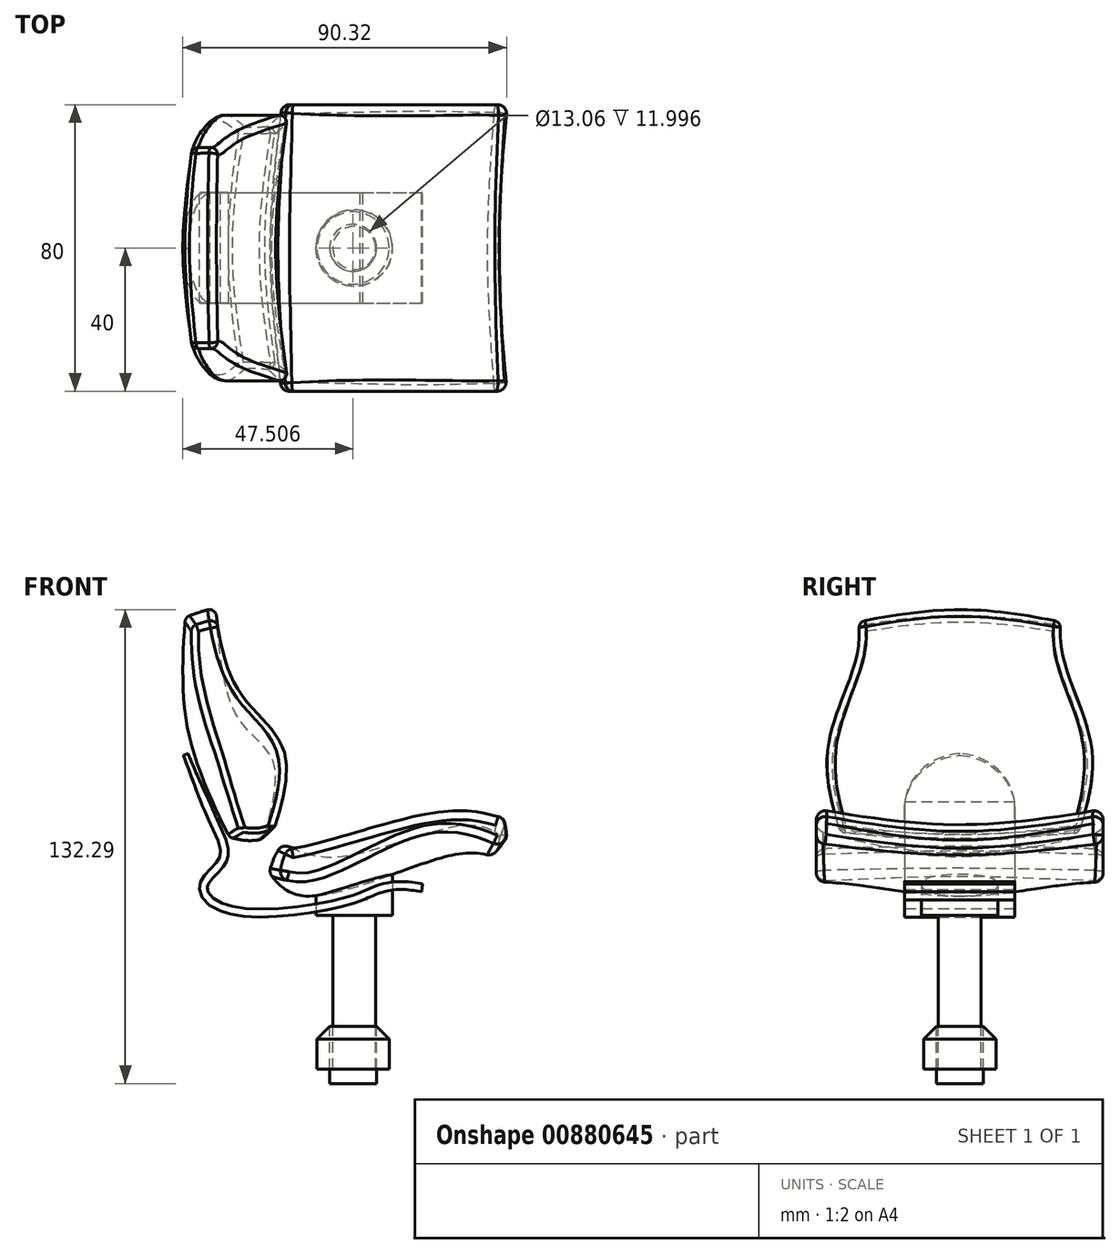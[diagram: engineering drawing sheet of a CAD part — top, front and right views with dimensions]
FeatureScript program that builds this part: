
annotation { "Feature Type Name" : "Feature", "Feature Type Description" : "" }
export const myFeature = defineFeature(function(context is Context, id is Id, definition is map)
    precondition{}
    {
        {
            var Q0;
            Q0=qCreatedBy(makeId("Front.planeOp"),FACE);
            var sketch = newSketch(context, id + "F0", { "sketchPlane" : qUnion([Q0])});
            skFitSpline(sketch, "E0", {"points": [v(-29.7, 59.89) * mm, v(-23.34, 27.8) * mm, v(-13.8, 16.24) * mm, v(-16.4, -6.3) * mm], "startDerivative": vector(6.88, -94.05) * mm, "endDerivative": vector(-21.45, -77.38) * mm});
            skFitSpline(sketch, "E1", {"points": [v(-37.8, 60.76) * mm, v(-37.5, 25.2) * mm, v(-25.36, -6.3) * mm], "startDerivative": vector(-5.51, -71.82) * mm, "endDerivative": vector(30.53, -62.27) * mm});
            skFitSpline(sketch, "E2", {"points": [v(-21.32, 59.89) * mm, v(-33.75, 57.58) * mm, v(-49.07, 50.93) * mm], "startDerivative": vector(-26.27, -3.23) * mm, "endDerivative": vector(-29.17, -14.43) * mm});
            skFitSpline(sketch, "E3", {"points": [v(-37.8, 0) * mm, v(-19.58, -6.3) * mm, v(-4.55, 0) * mm], "startDerivative": vector(35.9, -18.7) * mm, "endDerivative": vector(30.52, 19.22) * mm});
            skSolve(sketch);
        }
        {
            var Q0;
            Q0=qCreatedBy(makeId("Front.planeOp"),FACE);
            cPlane(context, id + "F1", {"entities" : qUnion([Q0]), "cplaneType" : CPlaneType.OFFSET, "offset" : 40 * mm, "width" : 150 * mm, "height" : 150 * mm});
        }
        {
            var Q0;
            Q0=qCreatedBy(id+"F1.planeOp",FACE);
            var sketch = newSketch(context, id + "F2", { "sketchPlane" : qUnion([Q0])});
            skFitSpline(sketch, "E4", {"points": [v(-32.08, 63.62) * mm, v(-23.6, 39.46) * mm, v(-9.8, 19.21) * mm, v(-15.3, -10.6) * mm], "startDerivative": vector(17.6, -78.26) * mm, "endDerivative": vector(-33.1, -90.51) * mm});
            skFitSpline(sketch, "E5", {"points": [v(-35.53, 62.05) * mm, v(-32.08, 31.45) * mm, v(-19.06, -10.92) * mm], "startDerivative": vector(3.9, -64.95) * mm, "endDerivative": vector(28.32, -80.51) * mm});
            skFitSpline(sketch, "E6", {"points": [v(-45.73, 44.8) * mm, v(-31.61, 52) * mm, v(-18.74, 51.23) * mm], "startDerivative": vector(26.78, 17.77) * mm, "endDerivative": vector(27.2, -5.3) * mm});
            skFitSpline(sketch, "E7", {"points": [v(-31.77, 0) * mm, v(-17.24, -3.37) * mm, v(-7.03, 1.29) * mm], "startDerivative": vector(28.52, -10.67) * mm, "endDerivative": vector(20.78, 13.83) * mm});
            skSolve(sketch);
        }
        {
            var Q0;
            Q0=qCreatedBy(makeId("Front.planeOp"),FACE);
            cPlane(context, id + "F3", {"entities" : qUnion([Q0]), "cplaneType" : CPlaneType.OFFSET, "offset" : 40 * mm, "oppositeDirection" : true, "width" : 150 * mm, "height" : 150 * mm});
        }
        {
            var Q0;
            Q0=qCreatedBy(id+"F3.planeOp",FACE);
            var sketch = newSketch(context, id + "F4", { "sketchPlane" : qUnion([Q0])});
            skFitSpline(sketch, "E8", {"points": [v(-32.11, 63.62) * mm, v(-23.64, 39.46) * mm, v(-9.83, 19.21) * mm, v(-15.32, -10.6) * mm], "startDerivative": vector(17.6, -78.26) * mm, "endDerivative": vector(-33.1, -90.51) * mm});
            skFitSpline(sketch, "E9", {"points": [v(-35.56, 62.05) * mm, v(-32.11, 31.45) * mm, v(-19.09, -10.92) * mm], "startDerivative": vector(3.9, -64.95) * mm, "endDerivative": vector(28.32, -80.51) * mm});
            skFitSpline(sketch, "E10", {"points": [v(-45.76, 44.8) * mm, v(-31.64, 52) * mm, v(-18.77, 51.23) * mm], "startDerivative": vector(26.78, 17.77) * mm, "endDerivative": vector(27.2, -5.3) * mm});
            skFitSpline(sketch, "E11", {"points": [v(-31.8, 0) * mm, v(-17.27, -3.37) * mm, v(-7.06, 1.29) * mm], "startDerivative": vector(28.52, -10.67) * mm, "endDerivative": vector(20.78, 13.83) * mm});
            skSolve(sketch);
        }
        {
            var Q0;
            {var subQ0=sQuery(id+"F2.wireOp",EDGE,"E6");var subQ1=sQuery(id+"F2.wireOp",EDGE,"E4");var subQ2=makeQuery(id+"F2.imprint","INTERSECT",VERTEX,{"derivedFrom":[subQ1,subQ0]});Q0=makeQuery(id+"F2.imprint","IMPRINT",FACE,{"disambiguationData":[TD([[makeQuery(id+"F2.imprint","IMPRINT",EDGE,{"disambiguationData":[TD([[subQ2,-1.0]])],"derivedFrom":subQ1}),-1.0]])]});}
            var Q1;
            {var subQ0=sQuery(id+"F0.wireOp",EDGE,"E2");var subQ1=sQuery(id+"F0.wireOp",EDGE,"E0");var subQ2=makeQuery(id+"F0.imprint","INTERSECT",VERTEX,{"derivedFrom":[subQ1,subQ0]});Q1=makeQuery(id+"F0.imprint","IMPRINT",FACE,{"disambiguationData":[TD([[makeQuery(id+"F0.imprint","IMPRINT",EDGE,{"disambiguationData":[TD([[subQ2,-1.0]])],"derivedFrom":subQ1}),-1.0]])]});}
            var Q2;
            {var subQ0=sQuery(id+"F4.wireOp",EDGE,"E10");var subQ1=sQuery(id+"F4.wireOp",EDGE,"E8");var subQ2=makeQuery(id+"F4.imprint","INTERSECT",VERTEX,{"derivedFrom":[subQ1,subQ0]});Q2=makeQuery(id+"F4.imprint","IMPRINT",FACE,{"disambiguationData":[TD([[makeQuery(id+"F4.imprint","IMPRINT",EDGE,{"disambiguationData":[TD([[subQ2,-1.0]])],"derivedFrom":subQ1}),-1.0]])]});}
            loft(context, id + "F5", {"sheetProfilesArray" : [{ "sheetProfileEntities" : qUnion([Q0]) }, { "sheetProfileEntities" : qUnion([Q1]) }, { "sheetProfileEntities" : qUnion([Q2]) }]});
        }
        {
            var Q0;
            Q0=qCreatedBy(makeId("Front.planeOp"),FACE);
            var sketch = newSketch(context, id + "F6", { "sketchPlane" : qUnion([Q0])});
            skFitSpline(sketch, "E12", {"points": [v(-11.23, -7.07) * mm, v(5.11, -10.79) * mm, v(40.37, -1.9) * mm, v(50.88, -5.45) * mm], "startDerivative": vector(45.5, -21.87) * mm, "endDerivative": vector(33.87, -22.99) * mm});
            skFitSpline(sketch, "E13", {"points": [v(-15.75, -13.7) * mm, v(-4.76, -21.79) * mm, v(36.65, -10.3) * mm, v(49.1, -11.11) * mm], "startDerivative": vector(29.25, -42.88) * mm, "endDerivative": vector(38.2, -11.88) * mm});
            skFitSpline(sketch, "E14", {"points": [v(49.1, 2.48) * mm, v(49.1, -8.36) * mm, v(44.41, -17.1) * mm], "startDerivative": vector(2.45, -22.05) * mm, "endDerivative": vector(-11.94, -17.05) * mm});
            skFitSpline(sketch, "E15", {"points": [v(-5.89, -1.24) * mm, v(-13.33, -11.11) * mm, v(-15.92, -24.37) * mm], "startDerivative": vector(-17.7, -18.78) * mm, "endDerivative": vector(-2.47, -27.42) * mm});
            skSolve(sketch);
        }
        {
            var Q0;
            Q0=qCreatedBy(makeId("Right.planeOp"),FACE);
            var sketch = newSketch(context, id + "F7", { "sketchPlane" : qUnion([Q0])});
            skFitSpline(sketch, "E16", {"points": [v(-31.84, 70.52) * mm, v(-28.4, 47.03) * mm, v(-36.85, 19.05) * mm, v(-29.2, -15) * mm], "startDerivative": vector(23.47, -77.15) * mm, "endDerivative": vector(36.54, -95.51) * mm});
            skLineSegment(sketch, "E17", {"start": v(-31.84, 70.52) * mm, "end": v(-59.81, 70.52) * mm});
            skLineSegment(sketch, "E18", {"start": v(-59.81, 70.52) * mm, "end": v(-59.81, -15) * mm});
            skLineSegment(sketch, "E19", {"start": v(-59.81, -15) * mm, "end": v(-29.2, -15) * mm});
            skLineSegment(sketch, "E20.MirrorCS", {"start": v(59.81, 70.52) * mm, "end": v(59.81, -15) * mm});
            skFitSpline(sketch, "E21.MirrorCS", {"points": [v(31.84, 70.52) * mm, v(28.4, 47.03) * mm, v(36.85, 19.05) * mm, v(29.2, -15) * mm], "startDerivative": vector(-23.47, -77.15) * mm, "endDerivative": vector(-36.54, -95.51) * mm});
            skLineSegment(sketch, "E22.MirrorCS", {"start": v(31.84, 70.52) * mm, "end": v(59.81, 70.52) * mm});
            skLineSegment(sketch, "E23.MirrorCS", {"start": v(59.81, -15) * mm, "end": v(29.2, -15) * mm});
            skSolve(sketch);
        }
        {
            var Q0;
            Q0=makeQuery(id+"F7.imprint","IMPRINT",FACE,{"disambiguationData":[TD([[makeQuery(id+"F7.imprint","IMPRINT",EDGE,{"derivedFrom":sQuery(id+"F7.wireOp",EDGE,"E16")}),-1.0]])]});
            var Q1;
            Q1=makeQuery(id+"F7.imprint","IMPRINT",FACE,{"disambiguationData":[TD([[makeQuery(id+"F7.imprint","IMPRINT",EDGE,{"derivedFrom":sQuery(id+"F7.wireOp",EDGE,"E20.MirrorCS")}),-1.0]])]});
            extrude(context, id + "F8", {"entities" : qUnion([Q0, Q1]), "operationType" : NewBodyOperationType.REMOVE, "endBound" : BoundingType.THROUGH_ALL, "oppositeDirection" : true, "depth" : 25 * mm, "offsetDistance" : 25 * mm, "hasSecondDirection" : true, "secondDirectionBound" : BoundingType.THROUGH_ALL, "secondDirectionOppositeDirection" : false, "secondDirectionDepth" : 25 * mm});
        }
        {
            var Q0;
            Q0=makeQuery(id+"F8.boolean.opBoolean","INTERSECT",EDGE,{"derivedFrom":[makeQuery(id+"F5.opLoft","SWEPT_FACE",FACE,{"disambiguationData":[OSD([sQuery(id+"F0.wireOp",EDGE,"E0"),sQuery(id+"F0.wireOp",EDGE,"E2"),sQuery(id+"F0.wireOp",EDGE,"E3"),sQuery(id+"F2.wireOp",EDGE,"E4"),sQuery(id+"F2.wireOp",EDGE,"E6"),sQuery(id+"F2.wireOp",EDGE,"E7"),sQuery(id+"F4.wireOp",EDGE,"E8"),sQuery(id+"F4.wireOp",EDGE,"E10"),sQuery(id+"F4.wireOp",EDGE,"E11")])]}),makeQuery(id+"F8.opExtrude","SWEPT_FACE",FACE,{"disambiguationData":[OSD([sQuery(id+"F7.wireOp",EDGE,"E16")])]})]});
            var Q1;
            Q1=makeQuery(id+"F8.boolean.opBoolean","INTERSECT",EDGE,{"derivedFrom":[makeQuery(id+"F5.opLoft","SWEPT_FACE",FACE,{"disambiguationData":[OSD([sQuery(id+"F0.wireOp",EDGE,"E0"),sQuery(id+"F0.wireOp",EDGE,"E2"),sQuery(id+"F0.wireOp",EDGE,"E3"),sQuery(id+"F2.wireOp",EDGE,"E4"),sQuery(id+"F2.wireOp",EDGE,"E6"),sQuery(id+"F2.wireOp",EDGE,"E7"),sQuery(id+"F4.wireOp",EDGE,"E8"),sQuery(id+"F4.wireOp",EDGE,"E10"),sQuery(id+"F4.wireOp",EDGE,"E11")])]}),makeQuery(id+"F8.opExtrude","SWEPT_FACE",FACE,{"disambiguationData":[OSD([sQuery(id+"F7.wireOp",EDGE,"E21.MirrorCS")])]})]});
            var Q2;
            Q2=makeQuery(id+"F8.boolean.opBoolean","INTERSECT",EDGE,{"derivedFrom":[makeQuery(id+"F5.opLoft","SWEPT_FACE",FACE,{"disambiguationData":[OSD([sQuery(id+"F0.wireOp",EDGE,"E1"),sQuery(id+"F0.wireOp",EDGE,"E2"),sQuery(id+"F0.wireOp",EDGE,"E3"),sQuery(id+"F2.wireOp",EDGE,"E5"),sQuery(id+"F2.wireOp",EDGE,"E6"),sQuery(id+"F2.wireOp",EDGE,"E7"),sQuery(id+"F4.wireOp",EDGE,"E9"),sQuery(id+"F4.wireOp",EDGE,"E10"),sQuery(id+"F4.wireOp",EDGE,"E11")])]}),makeQuery(id+"F8.opExtrude","SWEPT_FACE",FACE,{"disambiguationData":[OSD([sQuery(id+"F7.wireOp",EDGE,"E16")])]})]});
            var Q3;
            Q3=makeQuery(id+"F8.boolean.opBoolean","INTERSECT",EDGE,{"derivedFrom":[makeQuery(id+"F5.opLoft","SWEPT_FACE",FACE,{"disambiguationData":[OSD([sQuery(id+"F0.wireOp",EDGE,"E1"),sQuery(id+"F0.wireOp",EDGE,"E2"),sQuery(id+"F0.wireOp",EDGE,"E3"),sQuery(id+"F2.wireOp",EDGE,"E5"),sQuery(id+"F2.wireOp",EDGE,"E6"),sQuery(id+"F2.wireOp",EDGE,"E7"),sQuery(id+"F4.wireOp",EDGE,"E9"),sQuery(id+"F4.wireOp",EDGE,"E10"),sQuery(id+"F4.wireOp",EDGE,"E11")])]}),makeQuery(id+"F8.opExtrude","SWEPT_FACE",FACE,{"disambiguationData":[OSD([sQuery(id+"F7.wireOp",EDGE,"E21.MirrorCS")])]})]});
            var Q4;
            Q4=makeQuery(id+"F5.opLoft","SWEPT_FACE",FACE,{"disambiguationData":[OSD([sQuery(id+"F0.wireOp",EDGE,"E0"),sQuery(id+"F0.wireOp",EDGE,"E1"),sQuery(id+"F0.wireOp",EDGE,"E2"),sQuery(id+"F2.wireOp",EDGE,"E4"),sQuery(id+"F2.wireOp",EDGE,"E5"),sQuery(id+"F2.wireOp",EDGE,"E6"),sQuery(id+"F4.wireOp",EDGE,"E8"),sQuery(id+"F4.wireOp",EDGE,"E9"),sQuery(id+"F4.wireOp",EDGE,"E10")])]});
            var Q5;
            Q5=makeQuery(id+"F5.opLoft","SWEPT_FACE",FACE,{"disambiguationData":[OSD([sQuery(id+"F0.wireOp",EDGE,"E0"),sQuery(id+"F0.wireOp",EDGE,"E1"),sQuery(id+"F0.wireOp",EDGE,"E3"),sQuery(id+"F2.wireOp",EDGE,"E4"),sQuery(id+"F2.wireOp",EDGE,"E5"),sQuery(id+"F2.wireOp",EDGE,"E7"),sQuery(id+"F4.wireOp",EDGE,"E8"),sQuery(id+"F4.wireOp",EDGE,"E9"),sQuery(id+"F4.wireOp",EDGE,"E11")])]});
            fillet(context, id + "F9", {"entities" : qUnion([Q0, Q1, Q2, Q3, Q4, Q5]), "radius" : 2 * mm, "tangentPropagation" : true, "allowEdgeOverflow" : false});
        }
        {
            var Q0;
            Q0=qCreatedBy(id+"F1.planeOp",FACE);
            var sketch = newSketch(context, id + "F10", { "sketchPlane" : qUnion([Q0])});
            skFitSpline(sketch, "E24", {"points": [v(-15.6, -10.09) * mm, v(-4.4, -7.66) * mm, v(32.54, 2.23) * mm, v(52.7, 0) * mm], "startDerivative": vector(38.04, 6) * mm, "endDerivative": vector(55.26, -14.76) * mm});
            skFitSpline(sketch, "E25", {"points": [v(-21.58, -9.6) * mm, v(-5.16, -17.74) * mm, v(29, -3.93) * mm, v(54, -9.6) * mm], "startDerivative": vector(52.28, -46.95) * mm, "endDerivative": vector(71.5, -34.88) * mm});
            skFitSpline(sketch, "E26", {"points": [v(48.03, 7.83) * mm, v(51.57, -3.93) * mm, v(50.64, -20.16) * mm], "startDerivative": vector(9.8, -24.11) * mm, "endDerivative": vector(-4.25, -31.7) * mm});
            skFitSpline(sketch, "E27", {"points": [v(-3.48, 0) * mm, v(-10.75, -11.95) * mm, v(-11.13, -24.08) * mm], "startDerivative": vector(-17.5, -22.54) * mm, "endDerivative": vector(2.43, -25.65) * mm});
            skSolve(sketch);
        }
        {
            var Q0;
            Q0=qCreatedBy(id+"F3.planeOp",FACE);
            var sketch = newSketch(context, id + "F11", { "sketchPlane" : qUnion([Q0])});
            skFitSpline(sketch, "E28", {"points": [v(-15.47, -10.13) * mm, v(-4.27, -7.7) * mm, v(32.68, 2.19) * mm, v(52.83, -0.04) * mm], "startDerivative": vector(38.04, 6) * mm, "endDerivative": vector(55.26, -14.76) * mm});
            skFitSpline(sketch, "E29", {"points": [v(-21.44, -9.65) * mm, v(-5.02, -17.78) * mm, v(29.13, -3.97) * mm, v(54.14, -9.65) * mm], "startDerivative": vector(52.28, -46.95) * mm, "endDerivative": vector(71.5, -34.88) * mm});
            skFitSpline(sketch, "E30", {"points": [v(48.16, 7.79) * mm, v(51.71, -3.97) * mm, v(50.78, -20.2) * mm], "startDerivative": vector(9.8, -24.11) * mm, "endDerivative": vector(-4.25, -31.7) * mm});
            skFitSpline(sketch, "E31", {"points": [v(-3.34, -0.04) * mm, v(-10.62, -12) * mm, v(-11, -24.12) * mm], "startDerivative": vector(-17.5, -22.54) * mm, "endDerivative": vector(2.43, -25.65) * mm});
            skSolve(sketch);
        }
        {
            var Q0;
            {var subQ0=sQuery(id+"F10.wireOp",EDGE,"E26");var subQ1=sQuery(id+"F10.wireOp",EDGE,"E24");var subQ2=makeQuery(id+"F10.imprint","INTERSECT",VERTEX,{"derivedFrom":[subQ1,subQ0]});Q0=makeQuery(id+"F10.imprint","IMPRINT",FACE,{"disambiguationData":[TD([[makeQuery(id+"F10.imprint","IMPRINT",EDGE,{"disambiguationData":[TD([[subQ2,1.0]])],"derivedFrom":subQ1}),-1.0]])]});}
            var Q1;
            {var subQ0=sQuery(id+"F6.wireOp",EDGE,"E14");var subQ1=sQuery(id+"F6.wireOp",EDGE,"E12");var subQ2=makeQuery(id+"F6.imprint","INTERSECT",VERTEX,{"derivedFrom":[subQ1,subQ0]});Q1=makeQuery(id+"F6.imprint","IMPRINT",FACE,{"disambiguationData":[TD([[makeQuery(id+"F6.imprint","IMPRINT",EDGE,{"disambiguationData":[TD([[subQ2,1.0]])],"derivedFrom":subQ1}),-1.0]])]});}
            var Q2;
            {var subQ0=sQuery(id+"F11.wireOp",EDGE,"E30");var subQ1=sQuery(id+"F11.wireOp",EDGE,"E28");var subQ2=makeQuery(id+"F11.imprint","INTERSECT",VERTEX,{"derivedFrom":[subQ1,subQ0]});Q2=makeQuery(id+"F11.imprint","IMPRINT",FACE,{"disambiguationData":[TD([[makeQuery(id+"F11.imprint","IMPRINT",EDGE,{"disambiguationData":[TD([[subQ2,1.0]])],"derivedFrom":subQ1}),-1.0]])]});}
            loft(context, id + "F12", {"sheetProfilesArray" : [{ "sheetProfileEntities" : qUnion([Q0]) }, { "sheetProfileEntities" : qUnion([Q1]) }, { "sheetProfileEntities" : qUnion([Q2]) }]});
        }
        {
            var Q0;
            {var subQ0=sQuery(id+"F10.wireOp",EDGE,"E26");var subQ1=sQuery(id+"F10.wireOp",EDGE,"E24");var subQ2=makeQuery(id+"F10.imprint","INTERSECT",VERTEX,{"derivedFrom":[subQ1,subQ0]});Q0=makeQuery(id+"F12.opLoft","CAP_FACE",FACE,{"disambiguationData":[OSD([makeQuery(id+"F10.imprint","IMPRINT",FACE,{"disambiguationData":[TD([[makeQuery(id+"F10.imprint","IMPRINT",EDGE,{"disambiguationData":[TD([[subQ2,1.0]])],"derivedFrom":subQ1}),-1.0]])]})])],"isStart":true});}
            var Q1;
            Q1=makeQuery(id+"F12.opLoft","SWEPT_FACE",FACE,{"disambiguationData":[OSD([sQuery(id+"F6.wireOp",EDGE,"E12"),sQuery(id+"F6.wireOp",EDGE,"E13"),sQuery(id+"F6.wireOp",EDGE,"E14"),sQuery(id+"F10.wireOp",EDGE,"E24"),sQuery(id+"F10.wireOp",EDGE,"E25"),sQuery(id+"F10.wireOp",EDGE,"E26"),sQuery(id+"F11.wireOp",EDGE,"E28"),sQuery(id+"F11.wireOp",EDGE,"E29"),sQuery(id+"F11.wireOp",EDGE,"E30")])]});
            var Q2;
            {var subQ0=sQuery(id+"F11.wireOp",EDGE,"E30");var subQ1=sQuery(id+"F11.wireOp",EDGE,"E28");var subQ2=makeQuery(id+"F11.imprint","INTERSECT",VERTEX,{"derivedFrom":[subQ1,subQ0]});Q2=makeQuery(id+"F12.opLoft","CAP_FACE",FACE,{"disambiguationData":[OSD([makeQuery(id+"F11.imprint","IMPRINT",FACE,{"disambiguationData":[TD([[makeQuery(id+"F11.imprint","IMPRINT",EDGE,{"disambiguationData":[TD([[subQ2,1.0]])],"derivedFrom":subQ1}),-1.0]])]})])],"isStart":true});}
            var Q3;
            Q3=makeQuery(id+"F12.opLoft","SWEPT_FACE",FACE,{"disambiguationData":[OSD([sQuery(id+"F6.wireOp",EDGE,"E12"),sQuery(id+"F6.wireOp",EDGE,"E13"),sQuery(id+"F6.wireOp",EDGE,"E15"),sQuery(id+"F10.wireOp",EDGE,"E24"),sQuery(id+"F10.wireOp",EDGE,"E25"),sQuery(id+"F10.wireOp",EDGE,"E27"),sQuery(id+"F11.wireOp",EDGE,"E28"),sQuery(id+"F11.wireOp",EDGE,"E29"),sQuery(id+"F11.wireOp",EDGE,"E31")])]});
            fillet(context, id + "F13", {"entities" : qUnion([Q0, Q1, Q2, Q3]), "radius" : 2.5 * mm, "tangentPropagation" : true, "allowEdgeOverflow" : false});
        }
        {
            var Q0;
            Q0=qCreatedBy(makeId("Front.planeOp"),FACE);
            var sketch = newSketch(context, id + "F14", { "sketchPlane" : qUnion([Q0])});
            skFitSpline(sketch, "E32.0", {"points": [v(-38.66, 17.53) * mm, v(-37.9, 15.43) * mm, v(-36.74, 12.29) * mm, v(-35.2, 8.2) * mm, v(-34.04, 5.21) * mm, v(-33.08, 2.8) * mm, v(-32.3, 0.95) * mm, v(-31.72, -0.4) * mm, v(-31.14, -1.72) * mm, v(-30.36, -3.42) * mm, v(-29.45, -5.37) * mm, v(-28.78, -7.1) * mm, v(-28.45, -8.34) * mm, v(-28.33, -9.18) * mm, v(-28.33, -9.93) * mm, v(-28.42, -10.5) * mm, v(-28.57, -10.93) * mm, v(-28.76, -11.36) * mm, v(-29.13, -11.97) * mm, v(-29.74, -12.73) * mm, v(-30.46, -13.53) * mm, v(-31.24, -14.35) * mm, v(-32.04, -15.2) * mm, v(-32.8, -16.09) * mm, v(-33.36, -16.88) * mm, v(-33.74, -17.58) * mm, v(-33.97, -18.14) * mm, v(-34.13, -18.75) * mm, v(-34.23, -19.58) * mm, v(-34.12, -20.61) * mm, v(-33.67, -21.77) * mm, v(-32.98, -22.8) * mm, v(-31.77, -24.05) * mm, v(-30.2, -25.1) * mm, v(-28.3, -25.97) * mm, v(-26.72, -26.51) * mm, v(-25, -26.94) * mm, v(-22.57, -27.35) * mm, v(-19.3, -27.63) * mm, v(-15.11, -27.63) * mm, v(-10.84, -27.39) * mm, v(-6.61, -26.95) * mm, v(-2.6, -26.38) * mm, v(1.04, -25.74) * mm, v(4.17, -25.1) * mm, v(6.62, -24.5) * mm, v(9.18, -23.74) * mm, v(10.56, -23.22) * mm, v(11.45, -22.89) * mm]});
            skFitSpline(sketch, "E33.trimOffspring", {"points": [v(-37.34, 18) * mm, v(-27.32, -11.55) * mm, v(-32.73, -18.94) * mm, v(-25.86, -25.27) * mm, v(3.96, -23.69) * mm, v(10.95, -21.58) * mm], "startDerivative": vector(36.87, -100.49) * mm, "endDerivative": vector(42.5, 16.06) * mm});
            skPoint(sketch, "E34.endDerivative.orphan", {"position": v(9.21, -22.23) * mm});
            skFitSpline(sketch, "E35.0", {"points": [v(-36.6, 18.28) * mm, v(-35.83, 16.2) * mm, v(-34.67, 13.05) * mm, v(-33.14, 8.98) * mm, v(-32, 6.02) * mm, v(-30.85, 3.16) * mm, v(-29.9, 0.9) * mm, v(-29.13, -0.82) * mm, v(-28.37, -2.48) * mm, v(-27.44, -4.48) * mm, v(-26.7, -6.38) * mm, v(-26.3, -7.88) * mm, v(-26.13, -8.99) * mm, v(-26.12, -9.91) * mm, v(-26.21, -10.65) * mm, v(-26.34, -11.2) * mm, v(-26.52, -11.73) * mm, v(-26.76, -12.26) * mm, v(-27.04, -12.76) * mm, v(-27.36, -13.24) * mm, v(-27.7, -13.7) * mm, v(-28.2, -14.31) * mm, v(-28.86, -15.04) * mm, v(-29.66, -15.87) * mm, v(-30.41, -16.68) * mm, v(-31.08, -17.46) * mm, v(-31.5, -18.07) * mm, v(-31.75, -18.53) * mm, v(-31.86, -18.8) * mm, v(-31.92, -19.01) * mm, v(-31.96, -19.17) * mm, v(-31.98, -19.32) * mm, v(-32, -19.62) * mm, v(-31.97, -19.98) * mm, v(-31.84, -20.4) * mm, v(-31.64, -20.84) * mm, v(-31.27, -21.4) * mm, v(-30.4, -22.31) * mm, v(-29.12, -23.18) * mm, v(-27.49, -23.92) * mm, v(-25.64, -24.56) * mm, v(-22.94, -25.11) * mm, v(-19.2, -25.42) * mm, v(-15.18, -25.43) * mm, v(-9.63, -25.11) * mm, v(-4.14, -24.42) * mm, v(0.63, -23.58) * mm, v(3.7, -22.95) * mm, v(6.05, -22.37) * mm, v(7.88, -21.83) * mm, v(9.35, -21.33) * mm, v(10.22, -21) * mm, v(10.67, -20.83) * mm]});
            skFitSpline(sketch, "E36", {"points": [v(11.45, -22.89) * mm, v(19.58, -20.1) * mm, v(27.76, -20.58) * mm], "startDerivative": vector(15.96, 7.16) * mm, "endDerivative": vector(16.68, -2.58) * mm});
            skFitSpline(sketch, "E37.0", {"points": [v(10.54, -20.88) * mm, v(11.2, -20.58) * mm, v(12.56, -19.98) * mm, v(14.66, -19.11) * mm, v(16.49, -18.5) * mm, v(18, -18.13) * mm, v(18.97, -17.95) * mm, v(19.76, -17.85) * mm, v(20.54, -17.78) * mm, v(21.51, -17.75) * mm, v(22.66, -17.76) * mm, v(24.16, -17.86) * mm, v(25.99, -18.08) * mm, v(27.4, -18.3) * mm, v(28.1, -18.4) * mm]});
            skLineSegment(sketch, "E38", {"start": v(28.1, -18.4) * mm, "end": v(27.76, -20.58) * mm});
            skLineSegment(sketch, "E39", {"start": v(-36.6, 18.28) * mm, "end": v(-38.66, 17.53) * mm});
            skSolve(sketch);
        }
        {
            var Q0;
            Q0=qCreatedBy(makeId("Top.planeOp"),FACE);
            cPlane(context, id + "F15", {"entities" : qUnion([Q0]), "cplaneType" : CPlaneType.OFFSET, "offset" : 27.2 * mm, "oppositeDirection" : true, "width" : 150 * mm, "height" : 150 * mm});
        }
        {
            var Q0;
            Q0=qCreatedBy(id+"F15.planeOp",FACE);
            var sketch = newSketch(context, id + "F16", { "sketchPlane" : qUnion([Q0])});
            skCircle(sketch, "E40", {"center": v(8.98, 0) * mm, "radius": 10.68 * mm});
            skSolve(sketch);
        }
        {
            var Q0;
            Q0 = qSketchRegion(id + "F16", true);
            var Q1;
            Q1=makeQuery(id+"F12.opLoft","SWEPT_FACE",FACE,{"disambiguationData":[OSD([sQuery(id+"F6.wireOp",EDGE,"E13"),sQuery(id+"F6.wireOp",EDGE,"E14"),sQuery(id+"F6.wireOp",EDGE,"E15"),sQuery(id+"F10.wireOp",EDGE,"E25"),sQuery(id+"F10.wireOp",EDGE,"E26"),sQuery(id+"F10.wireOp",EDGE,"E27"),sQuery(id+"F11.wireOp",EDGE,"E29"),sQuery(id+"F11.wireOp",EDGE,"E30"),sQuery(id+"F11.wireOp",EDGE,"E31")])]});
            extrude(context, id + "F17", {"entities" : qUnion([Q0]), "endBound" : BoundingType.UP_TO_SURFACE, "depth" : 25 * mm, "endBoundEntityFace" : qUnion([Q1]), "offsetDistance" : 25 * mm});
        }
        {
            var Q0;
            Q0=makeQuery(id+"F14.imprint","IMPRINT",FACE,{"disambiguationData":[TD([[makeQuery(id+"F14.imprint","IMPRINT",EDGE,{"derivedFrom":sQuery(id+"F14.wireOp",EDGE,"E32.0")}),1.0]])]});
            extrude(context, id + "F18", {"entities" : qUnion([Q0]), "depth" : 30.8 * mm, "offsetDistance" : 25 * mm, "symmetric" : true});
        }
        {
            var Q0;
            Q0 = qSketchRegion(id + "F16", true);
            var Q1;
            Q1=makeQuery(id+"F12.opLoft","SWEPT_FACE",FACE,{"disambiguationData":[OSD([sQuery(id+"F6.wireOp",EDGE,"E13"),sQuery(id+"F6.wireOp",EDGE,"E14"),sQuery(id+"F6.wireOp",EDGE,"E15"),sQuery(id+"F10.wireOp",EDGE,"E25"),sQuery(id+"F10.wireOp",EDGE,"E26"),sQuery(id+"F10.wireOp",EDGE,"E27"),sQuery(id+"F11.wireOp",EDGE,"E29"),sQuery(id+"F11.wireOp",EDGE,"E30"),sQuery(id+"F11.wireOp",EDGE,"E31")])]});
            extrude(context, id + "F19", {"entities" : qUnion([Q0]), "flatOperationType" : FlatOperationType.REMOVE, "endBound" : BoundingType.UP_TO_SURFACE, "depth" : 25 * mm, "endBoundEntityFace" : qUnion([Q1]), "offsetDistance" : 25 * mm, "domain" : OperationDomain.MODEL});
        }
        {
            var Q0;
            Q0=makeQuery(id+"F18.opExtrude","CAP_EDGE",EDGE,{"disambiguationData":[OSD([sQuery(id+"F14.wireOp",EDGE,"E39")])],"isStart":false});
            var Q1;
            Q1=makeQuery(id+"F18.opExtrude","CAP_EDGE",EDGE,{"disambiguationData":[OSD([sQuery(id+"F14.wireOp",EDGE,"E39")])],"isStart":true});
            fillet(context, id + "F20", {"entities" : qUnion([Q0, Q1]), "radius" : 16.42 * mm, "tangentPropagation" : true, "allowEdgeOverflow" : false});
        }
        {
            var Q0;
            Q0=makeQuery(id+"F16.imprint","IMPRINT",FACE,{"disambiguationData":[TD([[makeQuery(id+"F16.imprint","IMPRINT",EDGE,{"derivedFrom":sQuery(id+"F16.wireOp",EDGE,"E40")}),1.0]])]});
            var sketch = newSketch(context, id + "F21", { "sketchPlane" : qUnion([Q0])});
            skCircle(sketch, "E41", {"center": v(8.98, 0) * mm, "radius": 6 * mm});
            skSolve(sketch);
        }
        {
            var Q0;
            Q0=makeQuery(id+"F21.imprint","IMPRINT",FACE,{"disambiguationData":[TD([[makeQuery(id+"F21.imprint","IMPRINT",EDGE,{"derivedFrom":sQuery(id+"F21.wireOp",EDGE,"E41")}),1.0]])]});
            extrude(context, id + "F22", {"entities" : qUnion([Q0]), "operationType" : NewBodyOperationType.ADD, "oppositeDirection" : true, "depth" : 42.9 * mm, "offsetDistance" : 25 * mm});
        }
        {
            var Q0;
            Q0=qCreatedBy(makeId("Front.planeOp"),FACE);
            var sketch = newSketch(context, id + "F23", { "sketchPlane" : qUnion([Q0])});
            skLineSegment(sketch, "E42.bottom", {"start": v(8.69, -70.18) * mm, "end": v(18.77, -70.18) * mm});
            skLineSegment(sketch, "E42.top", {"start": v(15.22, -56.74) * mm, "end": v(18.77, -56.74) * mm});
            skLineSegment(sketch, "E42.right", {"start": v(18.77, -70.18) * mm, "end": v(18.77, -56.74) * mm});
            skLineSegment(sketch, "E43.bottom", {"start": v(15.22, -67.92) * mm, "end": v(24.55, -67.92) * mm});
            skLineSegment(sketch, "E43.top", {"start": v(15.22, -74.14) * mm, "end": v(59.18, -74.14) * mm});
            skLineSegment(sketch, "E43.left", {"start": v(15.22, -67.92) * mm, "end": v(15.22, -74.14) * mm});
            skLineSegment(sketch, "E44", {"start": v(24.55, -67.92) * mm, "end": v(42.1, -70.51) * mm});
            skLineSegment(sketch, "E45", {"start": v(42.1, -70.51) * mm, "end": v(55.05, -69.4) * mm});
            skLineSegment(sketch, "E46", {"start": v(55.05, -69.4) * mm, "end": v(59.18, -74.14) * mm});
            skLineSegment(sketch, "E47.bottom", {"start": v(8.69, -70.18) * mm, "end": v(15.22, -70.18) * mm});
            skLineSegment(sketch, "E47.top", {"start": v(8.69, -74.14) * mm, "end": v(15.22, -74.14) * mm});
            skLineSegment(sketch, "E47.left", {"start": v(8.69, -70.18) * mm, "end": v(8.69, -74.14) * mm});
            skLineSegment(sketch, "E47.right", {"start": v(15.22, -70.18) * mm, "end": v(15.22, -74.14) * mm});
            skLineSegment(sketch, "E48.bottom", {"start": v(15.22, -70.18) * mm, "end": v(8.69, -70.18) * mm});
            skLineSegment(sketch, "E48.left", {"start": v(15.22, -70.18) * mm, "end": v(15.22, -56.74) * mm});
            skSolve(sketch);
        }
        {
            var Q0;
            {var subQ1=sQuery(id+"F23.wireOp",EDGE,"E42.bottom");Q0=makeQuery(id+"F23.imprint","IMPRINT",FACE,{"disambiguationData":[TD([[makeQuery(id+"F23.imprint","IMPRINT",EDGE,{"derivedFrom":subQ1}),-1.0]])]});}
            var Q1;
            Q1=makeQuery(id+"F23.imprint","IMPRINT",FACE,{"disambiguationData":[TD([[makeQuery(id+"F23.imprint","IMPRINT",EDGE,{"derivedFrom":sQuery(id+"F23.wireOp",EDGE,"E47.top")}),1.0]])]});
            var Q2;
            {var subQ0=sQuery(id+"F23.wireOp",EDGE,"E42.top");Q2=makeQuery(id+"F23.imprint","IMPRINT",FACE,{"disambiguationData":[TD([[makeQuery(id+"F23.imprint","IMPRINT",EDGE,{"derivedFrom":subQ0}),-1.0]])]});}
            var Q3;
            {var subQ0=sQuery(id+"F23.wireOp",EDGE,"E42.bottom");Q3=makeQuery(id+"F23.imprint","IMPRINT",FACE,{"disambiguationData":[TD([[makeQuery(id+"F23.imprint","IMPRINT",EDGE,{"derivedFrom":subQ0}),1.0]])]});}
            var Q4;
            Q4=sQuery(id+"F23.wireOp",EDGE,"E47.left");
            revolve(context, id + "F24", {"surfaceOperationType" : NewSurfaceOperationType.NEW, "entities" : qUnion([Q0, Q1, Q2, Q3]), "axis" : qUnion([Q4]), "revolveType" : RevolveType.FULL});
        }
        {
            var Q0;
            Q0=makeQuery(id+"F24.opRevolve","SWEPT_EDGE",EDGE,{"disambiguationData":[OSD([sQuery(id+"F23.wireOp",EDGE,"E42.top"),sQuery(id+"F23.wireOp",EDGE,"E42.right")])]});
            chamfer(context, id + "F25", {"entities" : qUnion([Q0]), "width" : 5 * mm, "tangentPropagation" : true});
        }
    });
